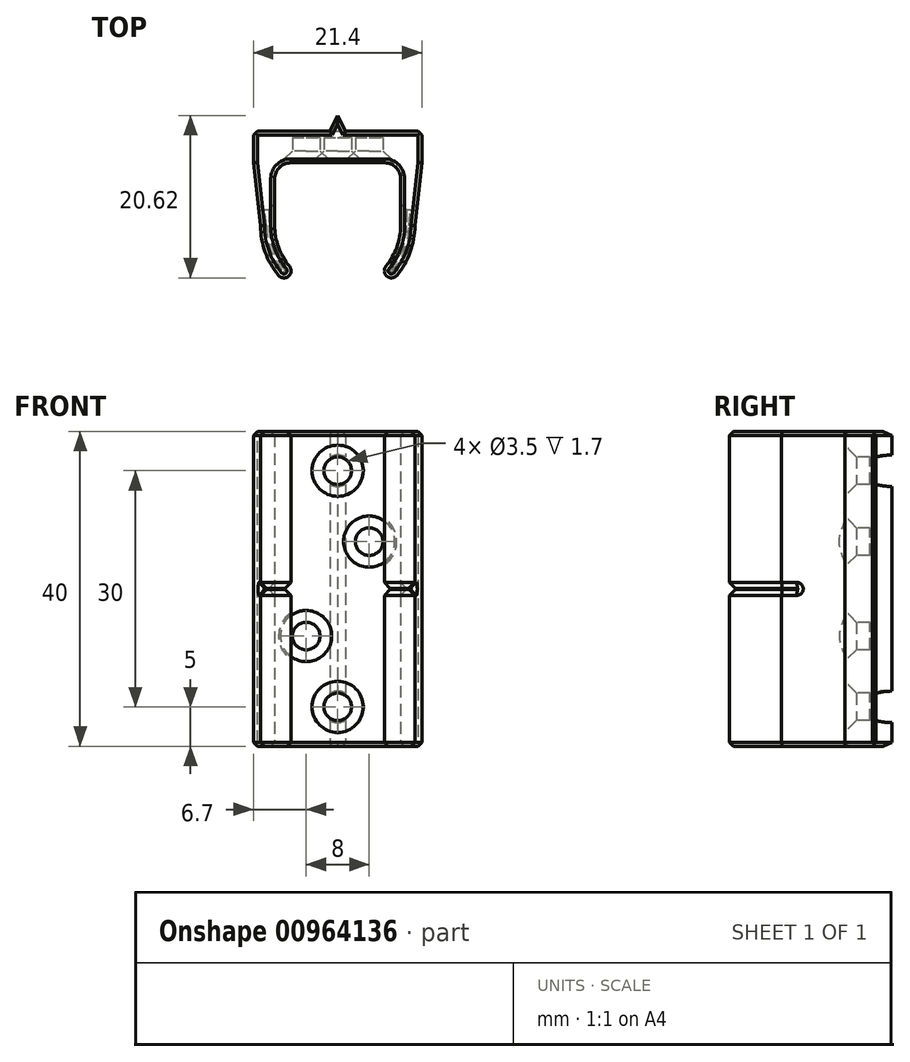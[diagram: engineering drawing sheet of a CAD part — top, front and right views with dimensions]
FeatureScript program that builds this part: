
annotation { "Feature Type Name" : "Feature", "Feature Type Description" : "" }
export const myFeature = defineFeature(function(context is Context, id is Id, definition is map)
    precondition{}
    {
        {
            var Q0;
            Q0=qCreatedBy(makeId("Top.planeOp"),FACE);
            var sketch = newSketch(context, id + "F0", { "sketchPlane" : qUnion([Q0])});
            skLineSegment(sketch, "E0", {"start": v(-10.7, 12) * mm, "end": v(-1, 12) * mm});
            skLineSegment(sketch, "E1", {"start": v(10.7, 12) * mm, "end": v(10.7, 8) * mm});
            skLineSegment(sketch, "E2", {"start": v(-10.7, 12) * mm, "end": v(-10.7, 8) * mm});
            skLineSegment(sketch, "E3", {"start": v(-1, 12) * mm, "end": v(0, 14) * mm});
            skLineSegment(sketch, "E4", {"start": v(0, 14) * mm, "end": v(1, 12) * mm});
            skLineSegment(sketch, "E5.trimOffspring", {"start": v(1, 12) * mm, "end": v(10.7, 12) * mm});
            skLineSegment(sketch, "E6", {"start": v(-8.05, -0.92) * mm, "end": v(-8.05, -0.92) * mm});
            skPoint(sketch, "E7.visualSharp", {"position": v(-10.7, 12) * mm});
            skPoint(sketch, "E8.visualSharp", {"position": v(10.7, 12) * mm});
            skLineSegment(sketch, "E9", {"start": v(0, 0) * mm, "end": v(-19.15, -16.07) * mm, "construction": true});
            skLineSegment(sketch, "E10", {"start": v(0, 0) * mm, "end": v(19.15, -16.07) * mm, "construction": true});
            skLineSegment(sketch, "E11", {"start": v(0, 0) * mm, "end": v(0, -25) * mm, "construction": true});
            skArc(sketch, "E12", {"start": v(6.13, -5.14) * mm, "mid": v(7.52, -2.74) * mm, "end": v(8, 0) * mm});
            skArc(sketch, "E13", {"start": v(-9.8, 0) * mm, "mid": v(-9.2, -3.35) * mm, "end": v(-7.5, -6.3) * mm});
            skLineSegment(sketch, "E14", {"start": v(-10.7, 8) * mm, "end": v(-9.8, 0) * mm});
            skLineSegment(sketch, "E15", {"start": v(10.7, 8) * mm, "end": v(9.8, 0) * mm});
            skArc(sketch, "E16.trimOffspring", {"start": v(7.5, -6.3) * mm, "mid": v(9.2, -3.35) * mm, "end": v(9.8, 0) * mm});
            skArc(sketch, "E17", {"start": v(-6.13, -5.14) * mm, "mid": v(-6.24, -6.41) * mm, "end": v(-7.5, -6.3) * mm});
            skArc(sketch, "E18", {"start": v(6.13, -5.14) * mm, "mid": v(6.24, -6.41) * mm, "end": v(7.5, -6.3) * mm});
            skLineSegment(sketch, "E19", {"start": v(-8, 0) * mm, "end": v(-8, 6) * mm});
            skLineSegment(sketch, "E20", {"start": v(8, 0) * mm, "end": v(8, 6) * mm});
            skLineSegment(sketch, "E21", {"start": v(-6, 8) * mm, "end": v(6, 8) * mm});
            skArc(sketch, "E22.trimOffspring", {"start": v(-8, 0) * mm, "mid": v(-7.52, -2.74) * mm, "end": v(-6.13, -5.14) * mm});
            skPoint(sketch, "E23.visualSharp", {"position": v(-8, 8) * mm});
            skArc(sketch, "E23.filletArc", {"start": v(-6, 8) * mm, "mid": v(-7.41, 7.41) * mm, "end": v(-8, 6) * mm});
            skPoint(sketch, "E24.visualSharp", {"position": v(8, 8) * mm});
            skArc(sketch, "E24.filletArc", {"start": v(8, 6) * mm, "mid": v(7.41, 7.41) * mm, "end": v(6, 8) * mm});
            skSolve(sketch);
        }
        {
            var Q0;
            Q0=qSketchRegion(id+"F0",true);
            extrude(context, id + "F1", {"entities" : qUnion([Q0]), "endBound" : BoundingType.SYMMETRIC, "depth" : 40 * mm, "offsetDistance" : 25 * mm});
        }
        {
            var Q0;
            Q0=qCreatedBy(makeId("Front.planeOp"),FACE);
            cPlane(context, id + "F2", {"entities" : qUnion([Q0]), "cplaneType" : CPlaneType.OFFSET, "offset" : 12 * mm, "oppositeDirection" : true, "width" : 150 * mm, "height" : 150 * mm});
        }
        {
            var Q0;
            Q0=qCreatedBy(makeId("Front.planeOp"),FACE);
            var sketch = newSketch(context, id + "F3", { "sketchPlane" : qUnion([Q0])});
            skCircle(sketch, "E25", {"center": v(0, 15) * mm, "radius": 1.75 * mm});
            skCircle(sketch, "E26", {"center": v(0, -15) * mm, "radius": 1.75 * mm});
            skCircle(sketch, "E27", {"center": v(4, 6) * mm, "radius": 1.75 * mm});
            skCircle(sketch, "E28", {"center": v(-4, -6) * mm, "radius": 1.75 * mm});
            skSolve(sketch);
        }
        {
            var Q0;
            Q0=qSketchRegion(id+"F3",true);
            extrude(context, id + "F4", {"entities" : qUnion([Q0]), "operationType" : NewBodyOperationType.REMOVE, "oppositeDirection" : true, "depth" : 11.2 * mm, "offsetDistance" : 25 * mm});
        }
        {
            var Q0;
            Q0=qCreatedBy(makeId("Front.planeOp"),FACE);
            var sketch = newSketch(context, id + "F5", { "sketchPlane" : qUnion([Q0])});
            skCircle(sketch, "E29", {"center": v(0, 15) * mm, "radius": 3.5 * mm});
            skCircle(sketch, "E30", {"center": v(4, 6) * mm, "radius": 3.5 * mm});
            skCircle(sketch, "E31", {"center": v(-4, -6) * mm, "radius": 3.5 * mm});
            skCircle(sketch, "E32", {"center": v(0, -15) * mm, "radius": 3.5 * mm});
            skSolve(sketch);
        }
        {
            var Q0;
            Q0=qSketchRegion(id+"F5",true);
            extrude(context, id + "F6", {"entities" : qUnion([Q0]), "operationType" : NewBodyOperationType.REMOVE, "oppositeDirection" : true, "depth" : 8 * mm, "offsetDistance" : 25 * mm});
        }
        {
            var Q0;
            Q0=makeQuery(id+"F4.boolean.opBoolean","INTERSECT",EDGE,{"derivedFrom":[makeQuery(id+"F1.opExtrude","SWEPT_FACE",FACE,{"disambiguationData":[OSD([sQuery(id+"F0.wireOp",EDGE,"E21")])]}),makeQuery(id+"F4.opExtrude","SWEPT_FACE",FACE,{"disambiguationData":[OSD([sQuery(id+"F3.wireOp",EDGE,"E26")])]})]});
            var Q1;
            Q1=makeQuery(id+"F4.boolean.opBoolean","INTERSECT",EDGE,{"derivedFrom":[makeQuery(id+"F1.opExtrude","SWEPT_FACE",FACE,{"disambiguationData":[OSD([sQuery(id+"F0.wireOp",EDGE,"E21")])]}),makeQuery(id+"F4.opExtrude","SWEPT_FACE",FACE,{"disambiguationData":[OSD([sQuery(id+"F3.wireOp",EDGE,"E28")])]})]});
            var Q2;
            Q2=makeQuery(id+"F4.boolean.opBoolean","INTERSECT",EDGE,{"derivedFrom":[makeQuery(id+"F1.opExtrude","SWEPT_FACE",FACE,{"disambiguationData":[OSD([sQuery(id+"F0.wireOp",EDGE,"E21")])]}),makeQuery(id+"F4.opExtrude","SWEPT_FACE",FACE,{"disambiguationData":[OSD([sQuery(id+"F3.wireOp",EDGE,"E25")])]})]});
            var Q3;
            Q3=makeQuery(id+"F4.boolean.opBoolean","INTERSECT",EDGE,{"derivedFrom":[makeQuery(id+"F1.opExtrude","SWEPT_FACE",FACE,{"disambiguationData":[OSD([sQuery(id+"F0.wireOp",EDGE,"E21")])]}),makeQuery(id+"F4.opExtrude","SWEPT_FACE",FACE,{"disambiguationData":[OSD([sQuery(id+"F3.wireOp",EDGE,"E27")])]})]});
            chamfer(context, id + "F7", {"entities" : qUnion([Q0, Q1, Q2, Q3]), "width" : 1.5 * mm, "tangentPropagation" : true});
        }
        {
            var Q0;
            Q0=makeQuery(id+"F1.opExtrude","CAP_EDGE",EDGE,{"disambiguationData":[OSD([sQuery(id+"F0.wireOp",EDGE,"E13")])],"isStart":true});
            var Q1;
            Q1=makeQuery(id+"F1.opExtrude","CAP_EDGE",EDGE,{"disambiguationData":[OSD([sQuery(id+"F0.wireOp",EDGE,"E12")])],"isStart":true});
            var Q2;
            Q2=makeQuery(id+"F1.opExtrude","CAP_EDGE",EDGE,{"disambiguationData":[OSD([sQuery(id+"F0.wireOp",EDGE,"E14")])],"isStart":true});
            var Q3;
            Q3=makeQuery(id+"F1.opExtrude","CAP_EDGE",EDGE,{"disambiguationData":[OSD([sQuery(id+"F0.wireOp",EDGE,"E0")])],"isStart":true});
            var Q4;
            Q4=makeQuery(id+"F1.opExtrude","CAP_EDGE",EDGE,{"disambiguationData":[OSD([sQuery(id+"F0.wireOp",EDGE,"E5.trimOffspring")])],"isStart":true});
            var Q5;
            Q5=makeQuery(id+"F1.opExtrude","CAP_EDGE",EDGE,{"disambiguationData":[OSD([sQuery(id+"F0.wireOp",EDGE,"E4")])],"isStart":true});
            var Q6;
            Q6=makeQuery(id+"F1.opExtrude","CAP_EDGE",EDGE,{"disambiguationData":[OSD([sQuery(id+"F0.wireOp",EDGE,"E3")])],"isStart":true});
            var Q7;
            Q7=makeQuery(id+"F1.opExtrude","CAP_EDGE",EDGE,{"disambiguationData":[OSD([sQuery(id+"F0.wireOp",EDGE,"E2")])],"isStart":true});
            var Q8;
            Q8=makeQuery(id+"F1.opExtrude","CAP_EDGE",EDGE,{"disambiguationData":[OSD([sQuery(id+"F0.wireOp",EDGE,"E17")])],"isStart":true});
            var Q9;
            Q9=makeQuery(id+"F1.opExtrude","CAP_EDGE",EDGE,{"disambiguationData":[OSD([sQuery(id+"F0.wireOp",EDGE,"E18")])],"isStart":true});
            var Q10;
            Q10=makeQuery(id+"F1.opExtrude","CAP_EDGE",EDGE,{"disambiguationData":[OSD([sQuery(id+"F0.wireOp",EDGE,"E16.trimOffspring")])],"isStart":true});
            var Q11;
            Q11=makeQuery(id+"F1.opExtrude","CAP_EDGE",EDGE,{"disambiguationData":[OSD([sQuery(id+"F0.wireOp",EDGE,"E15")])],"isStart":true});
            var Q12;
            Q12=makeQuery(id+"F1.opExtrude","CAP_EDGE",EDGE,{"disambiguationData":[OSD([sQuery(id+"F0.wireOp",EDGE,"E1")])],"isStart":true});
            var Q13;
            Q13=makeQuery(id+"F1.opExtrude","CAP_FACE",FACE,{"disambiguationData":[OSD([sQuery(id+"F0.wireOp",EDGE,"E0"),sQuery(id+"F0.wireOp",EDGE,"E1"),sQuery(id+"F0.wireOp",EDGE,"E2"),sQuery(id+"F0.wireOp",EDGE,"E3"),sQuery(id+"F0.wireOp",EDGE,"E4"),sQuery(id+"F0.wireOp",EDGE,"E5.trimOffspring"),sQuery(id+"F0.wireOp",EDGE,"E12"),sQuery(id+"F0.wireOp",EDGE,"E13"),sQuery(id+"F0.wireOp",EDGE,"E14"),sQuery(id+"F0.wireOp",EDGE,"E15"),sQuery(id+"F0.wireOp",EDGE,"E16.trimOffspring"),sQuery(id+"F0.wireOp",EDGE,"E17"),sQuery(id+"F0.wireOp",EDGE,"E18")])],"isStart":false});
            chamfer(context, id + "F8", {"entities" : qUnion([Q0, Q1, Q2, Q3, Q4, Q5, Q6, Q7, Q8, Q9, Q10, Q11, Q12, Q13]), "width" : .5 * mm, "tangentPropagation" : true});
        }
        {
            var Q0;
            Q0=makeQuery(id+"F1.opExtrude","SWEPT_EDGE",EDGE,{"disambiguationData":[OSD([sQuery(id+"F0.wireOp",EDGE,"E1"),sQuery(id+"F0.wireOp",EDGE,"E5.trimOffspring")])]});
            var Q1;
            Q1=makeQuery(id+"F1.opExtrude","SWEPT_EDGE",EDGE,{"disambiguationData":[OSD([sQuery(id+"F0.wireOp",EDGE,"E0"),sQuery(id+"F0.wireOp",EDGE,"E2")])]});
            chamfer(context, id + "F9", {"entities" : qUnion([Q0, Q1]), "width" : .5 * mm, "tangentPropagation" : true});
        }
        {
            var Q0;
            Q0=qCreatedBy(id+"F2.planeOp",FACE);
            var sketch = newSketch(context, id + "F10", { "sketchPlane" : qUnion([Q0])});
            skCircle(sketch, "E33", {"center": v(0, 15) * mm, "radius": 2 * mm});
            skCircle(sketch, "E34", {"center": v(0, -15) * mm, "radius": 2 * mm});
            skCircle(sketch, "E35", {"center": v(4, 6) * mm, "radius": 2 * mm});
            skCircle(sketch, "E36", {"center": v(-4, -6) * mm, "radius": 2 * mm});
            skSolve(sketch);
        }
        {
            var Q0;
            Q0=qSketchRegion(id+"F10",true);
            extrude(context, id + "F11", {"entities" : qUnion([Q0]), "operationType" : NewBodyOperationType.REMOVE, "oppositeDirection" : true, "depth" : 2 * mm, "offsetDistance" : 25 * mm});
        }
        {
            var Q0;
            Q0=qCreatedBy(makeId("Right.planeOp"),FACE);
            var sketch = newSketch(context, id + "F12", { "sketchPlane" : qUnion([Q0])});
            skLineSegment(sketch, "E37.bottom", {"start": v(-8, 0.07) * mm, "end": v(2, 0.07) * mm});
            skLineSegment(sketch, "E37.top", {"start": v(-8, -0.07) * mm, "end": v(2, -0.07) * mm});
            skLineSegment(sketch, "E37.left", {"start": v(-8, 0.07) * mm, "end": v(-8, -0.07) * mm});
            skArc(sketch, "E38", {"start": v(2, 0.07) * mm, "mid": v(2.08, 0) * mm, "end": v(2, -0.08) * mm});
            skSolve(sketch);
        }
        {
            var Q0;
            Q0=qSketchRegion(id+"F12",true);
            extrude(context, id + "F13", {"entities" : qUnion([Q0]), "operationType" : NewBodyOperationType.REMOVE, "endBound" : BoundingType.SYMMETRIC, "oppositeDirection" : true, "depth" : 25 * mm, "offsetDistance" : 25 * mm});
        }
        {
            var Q0;
            Q0=makeQuery(id+"F13.boolean.opBoolean","INTERSECT",EDGE,{"derivedFrom":[makeQuery(id+"F1.opExtrude","SWEPT_FACE",FACE,{"disambiguationData":[OSD([sQuery(id+"F0.wireOp",EDGE,"E16.trimOffspring")])]}),makeQuery(id+"F13.opExtrude","SWEPT_FACE",FACE,{"disambiguationData":[OSD([sQuery(id+"F12.wireOp",EDGE,"E37.top")])]})]});
            var Q1;
            Q1=makeQuery(id+"F13.boolean.opBoolean","INTERSECT",EDGE,{"derivedFrom":[makeQuery(id+"F1.opExtrude","SWEPT_FACE",FACE,{"disambiguationData":[OSD([sQuery(id+"F0.wireOp",EDGE,"E16.trimOffspring")])]}),makeQuery(id+"F13.opExtrude","SWEPT_FACE",FACE,{"disambiguationData":[OSD([sQuery(id+"F12.wireOp",EDGE,"E37.bottom")])]})]});
            var Q2;
            Q2=makeQuery(id+"F13.boolean.opBoolean","INTERSECT",EDGE,{"derivedFrom":[makeQuery(id+"F1.opExtrude","SWEPT_FACE",FACE,{"disambiguationData":[OSD([sQuery(id+"F0.wireOp",EDGE,"E15")])]}),makeQuery(id+"F13.opExtrude","SWEPT_FACE",FACE,{"disambiguationData":[OSD([sQuery(id+"F12.wireOp",EDGE,"E37.bottom")])]})]});
            var Q3;
            Q3=makeQuery(id+"F13.boolean.opBoolean","INTERSECT",EDGE,{"derivedFrom":[makeQuery(id+"F1.opExtrude","SWEPT_FACE",FACE,{"disambiguationData":[OSD([sQuery(id+"F0.wireOp",EDGE,"E15")])]}),makeQuery(id+"F13.opExtrude","SWEPT_FACE",FACE,{"disambiguationData":[OSD([sQuery(id+"F12.wireOp",EDGE,"E37.top")])]})]});
            var Q4;
            Q4=makeQuery(id+"F13.boolean.opBoolean","INTERSECT",EDGE,{"derivedFrom":[makeQuery(id+"F1.opExtrude","SWEPT_FACE",FACE,{"disambiguationData":[OSD([sQuery(id+"F0.wireOp",EDGE,"E22.trimOffspring")])]}),makeQuery(id+"F13.opExtrude","SWEPT_FACE",FACE,{"disambiguationData":[OSD([sQuery(id+"F12.wireOp",EDGE,"E37.top")])]})]});
            var Q5;
            Q5=makeQuery(id+"F13.boolean.opBoolean","INTERSECT",EDGE,{"derivedFrom":[makeQuery(id+"F1.opExtrude","SWEPT_FACE",FACE,{"disambiguationData":[OSD([sQuery(id+"F0.wireOp",EDGE,"E22.trimOffspring")])]}),makeQuery(id+"F13.opExtrude","SWEPT_FACE",FACE,{"disambiguationData":[OSD([sQuery(id+"F12.wireOp",EDGE,"E37.bottom")])]})]});
            var Q6;
            Q6=makeQuery(id+"F13.boolean.opBoolean","INTERSECT",EDGE,{"derivedFrom":[makeQuery(id+"F1.opExtrude","SWEPT_FACE",FACE,{"disambiguationData":[OSD([sQuery(id+"F0.wireOp",EDGE,"E19")])]}),makeQuery(id+"F13.opExtrude","SWEPT_FACE",FACE,{"disambiguationData":[OSD([sQuery(id+"F12.wireOp",EDGE,"E37.bottom")])]})]});
            var Q7;
            Q7=makeQuery(id+"F13.boolean.opBoolean","INTERSECT",EDGE,{"derivedFrom":[makeQuery(id+"F1.opExtrude","SWEPT_FACE",FACE,{"disambiguationData":[OSD([sQuery(id+"F0.wireOp",EDGE,"E19")])]}),makeQuery(id+"F13.opExtrude","SWEPT_FACE",FACE,{"disambiguationData":[OSD([sQuery(id+"F12.wireOp",EDGE,"E37.top")])]})]});
            var Q8;
            Q8=makeQuery(id+"F13.boolean.opBoolean","INTERSECT",EDGE,{"derivedFrom":[makeQuery(id+"F1.opExtrude","SWEPT_FACE",FACE,{"disambiguationData":[OSD([sQuery(id+"F0.wireOp",EDGE,"E19")])]}),makeQuery(id+"F13.opExtrude","SWEPT_FACE",FACE,{"disambiguationData":[OSD([sQuery(id+"F12.wireOp",EDGE,"E38")])]})]});
            var Q9;
            Q9=makeQuery(id+"F13.boolean.opBoolean","INTERSECT",EDGE,{"derivedFrom":[makeQuery(id+"F1.opExtrude","SWEPT_FACE",FACE,{"disambiguationData":[OSD([sQuery(id+"F0.wireOp",EDGE,"E14")])]}),makeQuery(id+"F13.opExtrude","SWEPT_FACE",FACE,{"disambiguationData":[OSD([sQuery(id+"F12.wireOp",EDGE,"E38")])]})]});
            var Q10;
            Q10=makeQuery(id+"F13.boolean.opBoolean","INTERSECT",EDGE,{"derivedFrom":[makeQuery(id+"F1.opExtrude","SWEPT_FACE",FACE,{"disambiguationData":[OSD([sQuery(id+"F0.wireOp",EDGE,"E14")])]}),makeQuery(id+"F13.opExtrude","SWEPT_FACE",FACE,{"disambiguationData":[OSD([sQuery(id+"F12.wireOp",EDGE,"E37.bottom")])]})]});
            chamfer(context, id + "F14", {"entities" : qUnion([Q0, Q1, Q2, Q3, Q4, Q5, Q6, Q7, Q8, Q9, Q10]), "width" : .75 * mm, "tangentPropagation" : true});
        }
    });
